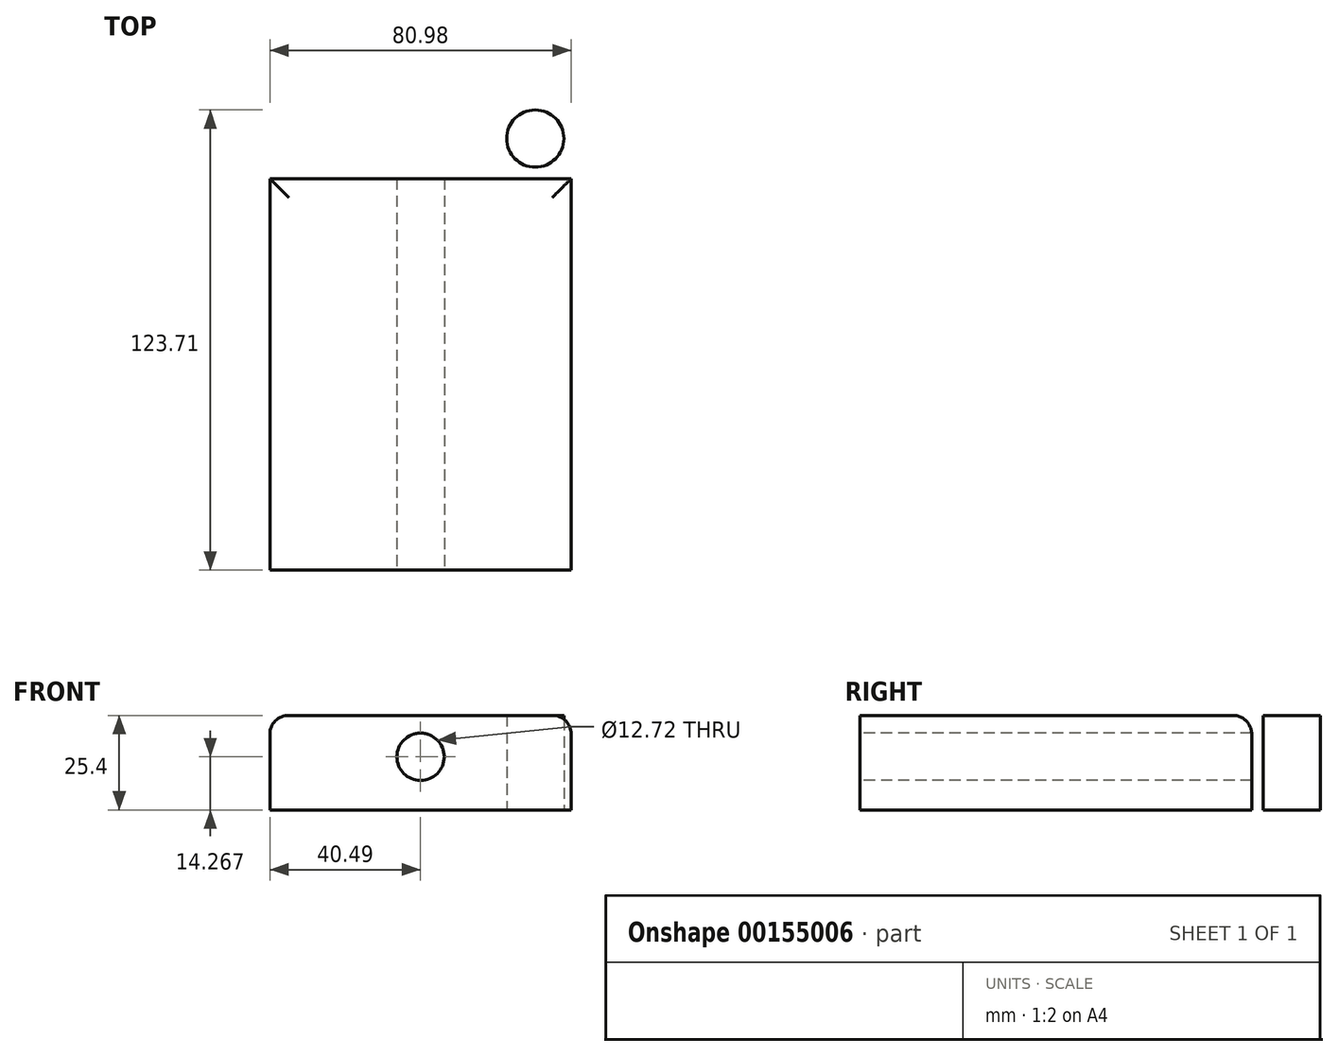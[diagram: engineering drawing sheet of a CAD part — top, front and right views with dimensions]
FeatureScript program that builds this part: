
annotation { "Feature Type Name" : "Feature", "Feature Type Description" : "" }
export const myFeature = defineFeature(function(context is Context, id is Id, definition is map)
    precondition{}
    {
        {
            var Q0;
            Q0=qCreatedBy(makeId("Top.planeOp"),FACE);
            var sketch = newSketch(context, id + "F0", { "sketchPlane" : qUnion([Q0])});
            skLineSegment(sketch, "E0", {"start": v(0, 52.63) * mm, "end": v(-40.49, 52.63) * mm});
            skLineSegment(sketch, "E1", {"start": v(-40.49, 52.63) * mm, "end": v(-40.49, 0) * mm});
            skLineSegment(sketch, "E2.MirrorCS", {"start": v(40.49, 52.63) * mm, "end": v(40.49, 0) * mm});
            skLineSegment(sketch, "E3.MirrorCS", {"start": v(0, 52.63) * mm, "end": v(40.49, 52.63) * mm});
            skLineSegment(sketch, "E4.MirrorCS", {"start": v(-40.49, -52.63) * mm, "end": v(-40.49, 0) * mm});
            skLineSegment(sketch, "E5.MirrorCS", {"start": v(0, -52.63) * mm, "end": v(-40.49, -52.63) * mm});
            skLineSegment(sketch, "E6.MirrorCS", {"start": v(0, -52.63) * mm, "end": v(40.49, -52.63) * mm});
            skLineSegment(sketch, "E7.MirrorCS", {"start": v(40.49, -52.63) * mm, "end": v(40.49, 0) * mm});
            skLineSegment(sketch, "E8", {"start": v(-41.48, 65.94) * mm, "end": v(-9.61, 65.94) * mm});
            skLineSegment(sketch, "E9", {"start": v(-40.1, 58.03) * mm, "end": v(-8.23, 58.03) * mm});
            skCircle(sketch, "E10", {"center": v(30.81, 63.4) * mm, "radius": 7.68 * mm});
            skLineSegment(sketch, "E11", {"start": v(25.83, 72.3) * mm, "end": v(44.15, 68.44) * mm});
            skSolve(sketch);
        }
        {
            var Q0;
            Q0 = qSketchRegion(id + "F0", true);
            extrude(context, id + "F1", {"entities" : qUnion([Q0]), "depth" : 25.4 * mm});
        }
        {
            var Q0;
            Q0=makeQuery(id+"F1.opExtrude","SWEPT_FACE",FACE,{"disambiguationData":[OSD([sQuery(id+"F0.wireOp",EDGE,"E5.MirrorCS"),sQuery(id+"F0.wireOp",EDGE,"E6.MirrorCS")])]});
            var sketch = newSketch(context, id + "F2", { "sketchPlane" : qUnion([Q0])});
            skCircle(sketch, "E12", {"center": v(0, 14.27) * mm, "radius": 6.36 * mm});
            skSolve(sketch);
        }
        {
            var Q0;
            Q0 = qSketchRegion(id + "F2", true);
            extrude(context, id + "F3", {"entities" : qUnion([Q0]), "operationType" : NewBodyOperationType.REMOVE, "oppositeDirection" : true, "depth" : 119.38 * mm});
        }
        {
            var Q0;
            Q0=makeQuery(id+"F1.opExtrude","CAP_EDGE",EDGE,{"disambiguationData":[OSD([sQuery(id+"F0.wireOp",EDGE,"E0"),sQuery(id+"F0.wireOp",EDGE,"E3.MirrorCS")])],"isStart":false});
            var Q1;
            Q1=makeQuery(id+"F1.opExtrude","CAP_EDGE",EDGE,{"disambiguationData":[OSD([sQuery(id+"F0.wireOp",EDGE,"E1"),sQuery(id+"F0.wireOp",EDGE,"E4.MirrorCS")])],"isStart":false});
            var Q2;
            Q2=makeQuery(id+"F1.opExtrude","CAP_EDGE",EDGE,{"disambiguationData":[OSD([sQuery(id+"F0.wireOp",EDGE,"E2.MirrorCS"),sQuery(id+"F0.wireOp",EDGE,"E7.MirrorCS")])],"isStart":false});
            fillet(context, id + "F4", {"entities" : qUnion([Q0, Q1, Q2]), "radius" : 5.08 * mm, "tangentPropagation" : true, "allowEdgeOverflow" : false});
        }
    });
